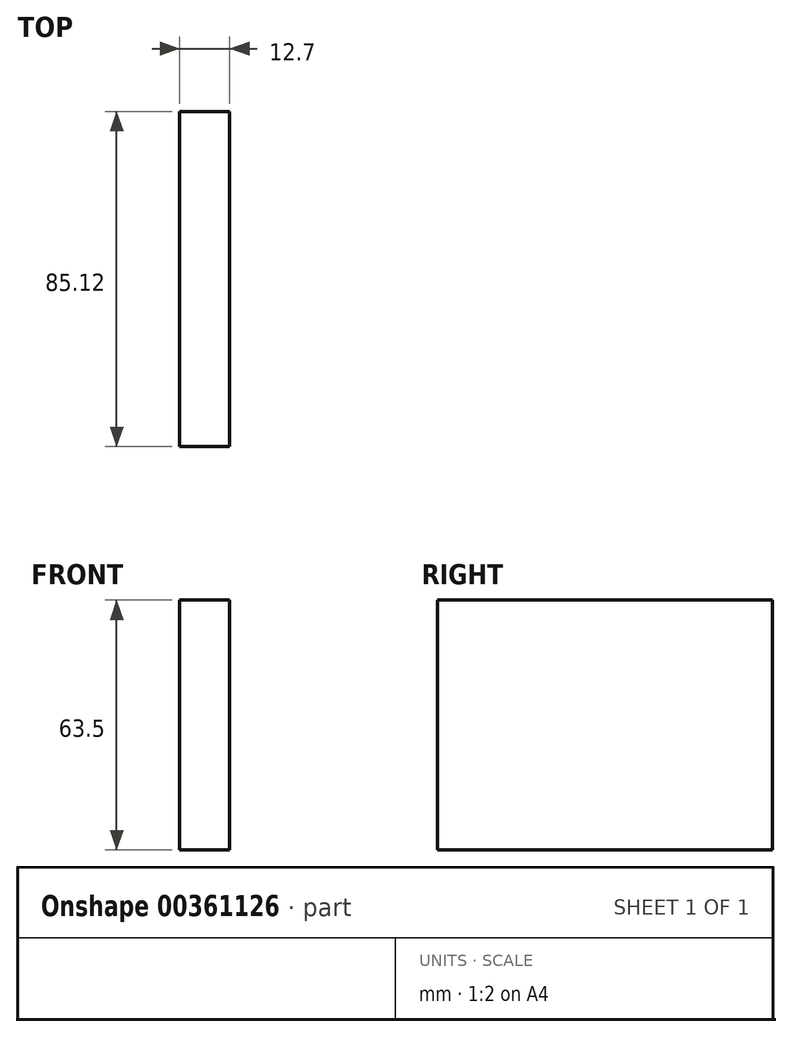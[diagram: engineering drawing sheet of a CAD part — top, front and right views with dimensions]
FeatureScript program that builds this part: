
annotation { "Feature Type Name" : "Feature", "Feature Type Description" : "" }
export const myFeature = defineFeature(function(context is Context, id is Id, definition is map)
    precondition{}
    {
        {
            var Q0;
            Q0=qCreatedBy(makeId("Front.planeOp"),FACE);
            var sketch = newSketch(context, id + "F0", { "sketchPlane" : qUnion([Q0])});
            skLineSegment(sketch, "E0.bottom", {"start": v(0, 0) * mm, "end": v(12.7, 0) * mm});
            skLineSegment(sketch, "E0.top", {"start": v(0, -63.5) * mm, "end": v(12.7, -63.5) * mm});
            skLineSegment(sketch, "E0.left", {"start": v(0, 0) * mm, "end": v(0, -63.5) * mm});
            skLineSegment(sketch, "E0.right", {"start": v(12.7, 0) * mm, "end": v(12.7, -63.5) * mm});
            skSolve(sketch);
        }
        {
            var Q0;
            Q0 = qSketchRegion(id + "F0", true);
            extrude(context, id + "F1", {"entities" : qUnion([Q0]), "depth" : 85.12 * mm});
        }
    });
